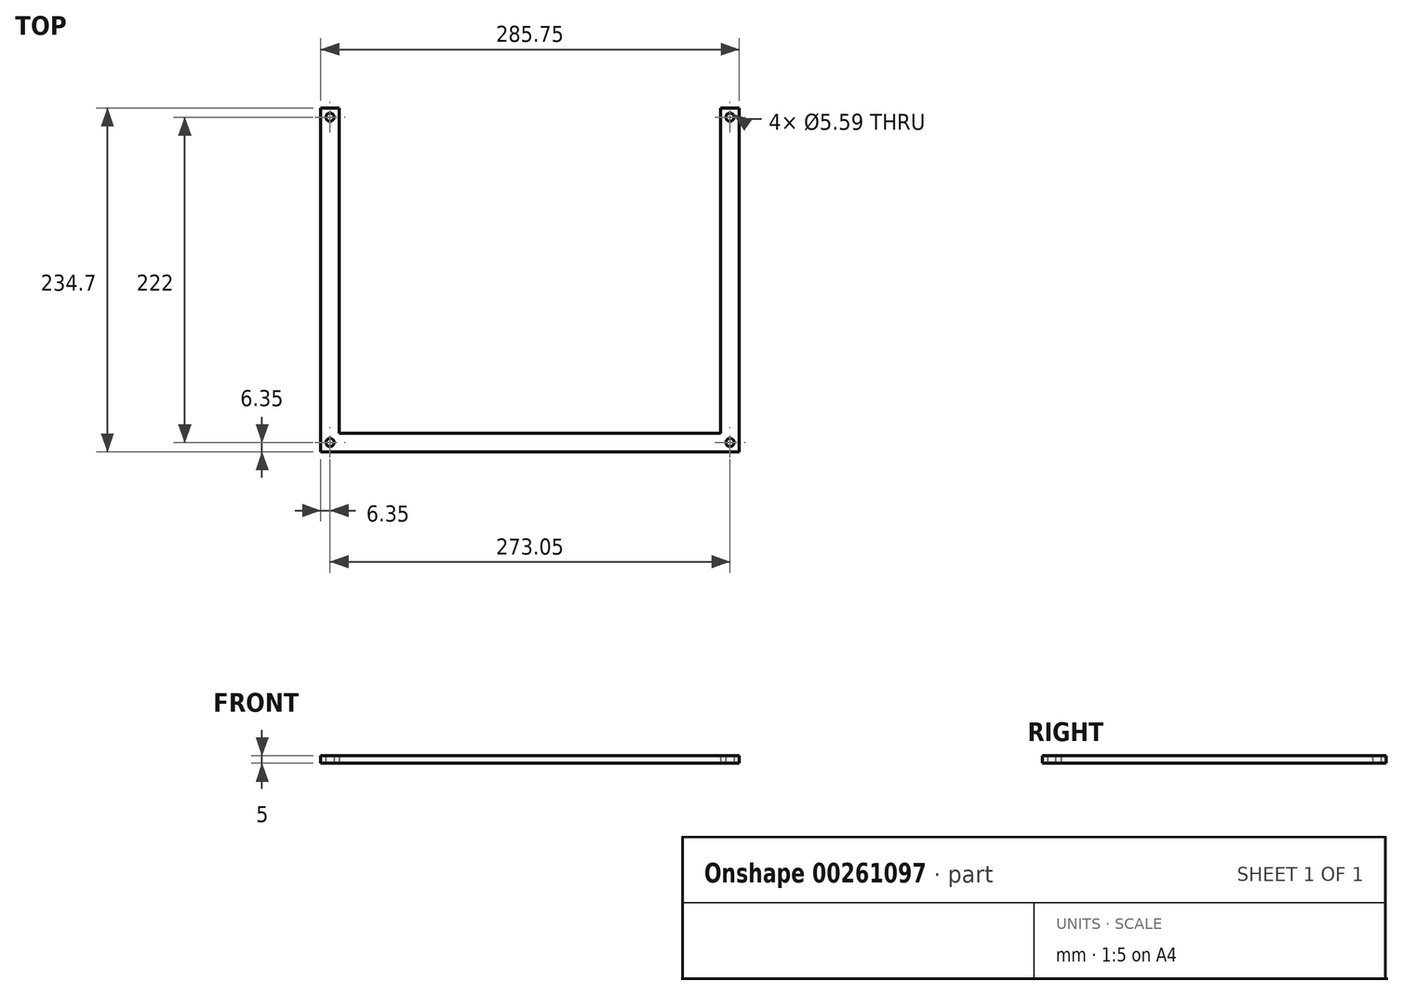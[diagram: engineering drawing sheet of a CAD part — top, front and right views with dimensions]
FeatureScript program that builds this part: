
annotation { "Feature Type Name" : "Feature", "Feature Type Description" : "" }
export const myFeature = defineFeature(function(context is Context, id is Id, definition is map)
    precondition{}
    {
        {
            var Q0;
            Q0=qCreatedBy(makeId("Top.planeOp"),FACE);
            var sketch = newSketch(context, id + "F0", { "sketchPlane" : qUnion([Q0])});
            skLineSegment(sketch, "E0.bottom", {"start": v(-6.35, 117.35) * mm, "end": v(6.35, 117.35) * mm});
            skLineSegment(sketch, "E0.top", {"start": v(-6.35, -117.35) * mm, "end": v(6.35, -117.35) * mm});
            skLineSegment(sketch, "E0.left", {"start": v(-6.35, 117.35) * mm, "end": v(-6.35, -117.35) * mm});
            skLineSegment(sketch, "E0.right", {"start": v(6.35, 117.35) * mm, "end": v(6.35, -117.35) * mm});
            skPoint(sketch, "E0.middle", {"position": v(0, 0) * mm});
            skPoint(sketch, "E1.centerSnap0", {"position": v(0, 117.35) * mm});
            skCircle(sketch, "E2", {"center": v(0, 111) * mm, "radius": 2.8 * mm});
            skCircle(sketch, "E3", {"center": v(0, -111) * mm, "radius": 2.8 * mm});
            skLineSegment(sketch, "E4.bottom", {"start": v(6.35, -117.35) * mm, "end": v(266.7, -117.35) * mm});
            skLineSegment(sketch, "E4.top", {"start": v(6.35, -104.65) * mm, "end": v(266.7, -104.65) * mm});
            skLineSegment(sketch, "E4.right", {"start": v(266.7, -117.35) * mm, "end": v(266.7, -104.65) * mm});
            skLineSegment(sketch, "E5.bottom", {"start": v(266.7, 117.35) * mm, "end": v(279.4, 117.35) * mm});
            skLineSegment(sketch, "E5.top", {"start": v(266.7, -117.35) * mm, "end": v(279.4, -117.35) * mm});
            skLineSegment(sketch, "E5.left", {"start": v(266.7, 117.35) * mm, "end": v(266.7, -104.65) * mm});
            skLineSegment(sketch, "E5.right", {"start": v(279.4, 117.35) * mm, "end": v(279.4, -117.35) * mm});
            skPoint(sketch, "E5.middle", {"position": v(273.05, 0) * mm});
            skPoint(sketch, "E6.centerSnap0", {"position": v(273.05, 117.35) * mm});
            skCircle(sketch, "E7", {"center": v(273.05, 111) * mm, "radius": 2.8 * mm});
            skCircle(sketch, "E8", {"center": v(273.05, -111) * mm, "radius": 2.8 * mm});
            skSolve(sketch);
        }
        {
            var Q0;
            Q0=makeQuery(id+"F0.imprint","IMPRINT",FACE,{"disambiguationData":[TD([[makeQuery(id+"F0.imprint","IMPRINT",EDGE,{"derivedFrom":sQuery(id+"F0.wireOp",EDGE,"E0.bottom")}),-1.0]])]});
            var Q1;
            Q1=makeQuery(id+"F0.imprint","IMPRINT",FACE,{"disambiguationData":[TD([[makeQuery(id+"F0.imprint","IMPRINT",EDGE,{"derivedFrom":sQuery(id+"F0.wireOp",EDGE,"E4.right")}),-1.0]])]});
            var Q2;
            {var subQ0=sQuery(id+"F0.wireOp",EDGE,"E4.bottom");Q2=makeQuery(id+"F0.imprint","IMPRINT",FACE,{"disambiguationData":[TD([[makeQuery(id+"F0.imprint","IMPRINT",EDGE,{"derivedFrom":subQ0}),1.0]])]});}
            extrude(context, id + "F1", {"entities" : qUnion([Q0, Q1, Q2]), "depth" : 5 * mm});
        }
    });
